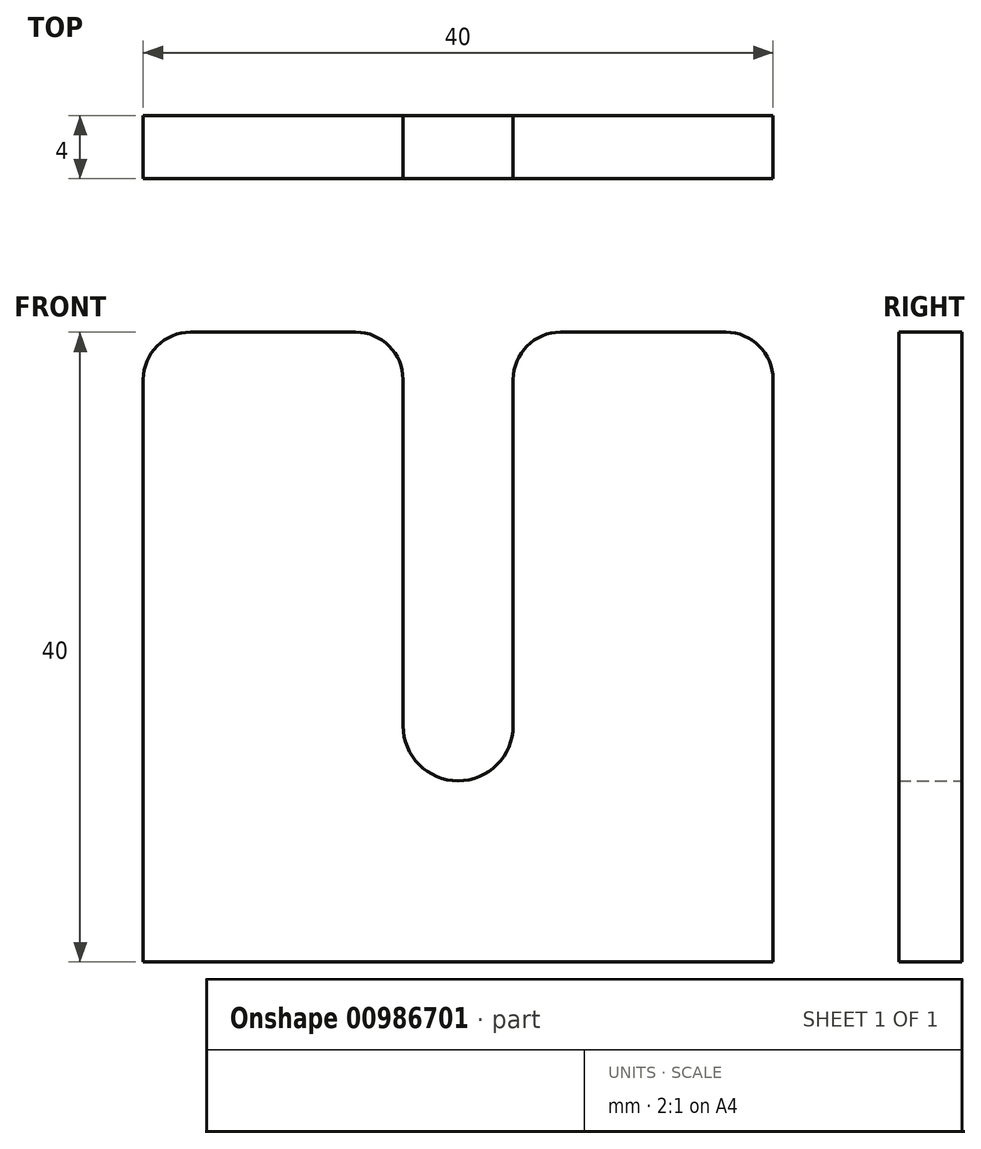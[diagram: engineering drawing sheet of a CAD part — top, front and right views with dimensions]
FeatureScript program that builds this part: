
annotation { "Feature Type Name" : "Feature", "Feature Type Description" : "" }
export const myFeature = defineFeature(function(context is Context, id is Id, definition is map)
    precondition{}
    {
        {
            var Q0;
            Q0=qCreatedBy(makeId("Front.planeOp"),FACE);
            var sketch = newSketch(context, id + "F0", { "sketchPlane" : qUnion([Q0])});
            skLineSegment(sketch, "E0.bottom", {"start": v(-20, -20) * mm, "end": v(20, -20) * mm});
            skLineSegment(sketch, "E0.top", {"start": v(-17, 20) * mm, "end": v(-6.5, 20) * mm});
            skLineSegment(sketch, "E0.left", {"start": v(-20, -20) * mm, "end": v(-20, 17) * mm});
            skLineSegment(sketch, "E0.right", {"start": v(20, -20) * mm, "end": v(20, 17) * mm});
            skPoint(sketch, "E0.middle", {"position": v(0, 0) * mm});
            skLineSegment(sketch, "E1", {"start": v(0, 20) * mm, "end": v(0, -5) * mm});
            skArc(sketch, "E2", {"start": v(-3.5, -5) * mm, "mid": v(0, -8.5) * mm, "end": v(3.5, -5) * mm});
            skLineSegment(sketch, "E3.0", {"start": v(3.5, 17) * mm, "end": v(3.5, -5) * mm});
            skLineSegment(sketch, "E4.0", {"start": v(-3.5, 17) * mm, "end": v(-3.5, -5) * mm});
            skLineSegment(sketch, "E5.trimOffspring", {"start": v(6.5, 20) * mm, "end": v(17, 20) * mm});
            skPoint(sketch, "E6.visualSharp", {"position": v(-3.5, 20) * mm});
            skArc(sketch, "E6.filletArc", {"start": v(-3.5, 17) * mm, "mid": v(-4.38, 19.12) * mm, "end": v(-6.5, 20) * mm});
            skPoint(sketch, "E7.visualSharp", {"position": v(-20, 20) * mm});
            skArc(sketch, "E7.filletArc", {"start": v(-17, 20) * mm, "mid": v(-19.12, 19.12) * mm, "end": v(-20, 17) * mm});
            skPoint(sketch, "E8.visualSharp", {"position": v(3.5, 20) * mm});
            skArc(sketch, "E8.filletArc", {"start": v(6.5, 20) * mm, "mid": v(4.38, 19.12) * mm, "end": v(3.5, 17) * mm});
            skPoint(sketch, "E9.visualSharp", {"position": v(20, 20) * mm});
            skArc(sketch, "E9.filletArc", {"start": v(20, 17) * mm, "mid": v(19.12, 19.12) * mm, "end": v(17, 20) * mm});
            skSolve(sketch);
        }
        {
            var Q0;
            Q0=makeQuery(id+"F0.imprint","IMPRINT",FACE,{"disambiguationData":[TD([[makeQuery(id+"F0.imprint","IMPRINT",EDGE,{"derivedFrom":sQuery(id+"F0.wireOp",EDGE,"E0.bottom")}),1.0]])]});
            extrude(context, id + "F1", {"entities" : qUnion([Q0]), "depth" : 4 * mm, "offsetDistance" : 25 * mm});
        }
    });
